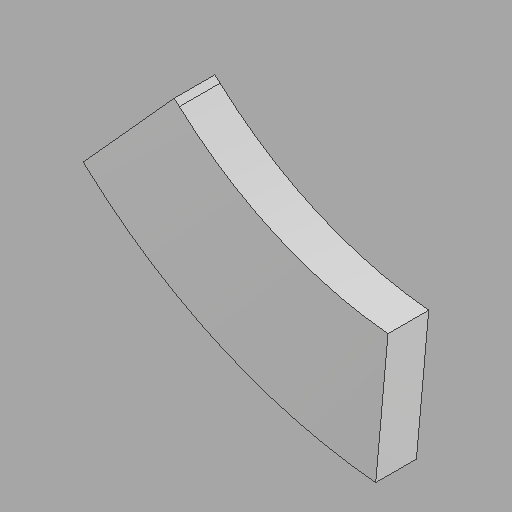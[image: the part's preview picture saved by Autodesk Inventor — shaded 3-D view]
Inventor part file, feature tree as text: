
AUTODESK INVENTOR PART (.ipt)
format: ipt  version: 2022.1 (Build 261234020, 234B)  size: 91,648 bytes
history: imported  units: in
note: dims shown in document units (in); Inventor stores cm internally (conversion verified against a paired STEP export)
features: imported_body x1
ambient origin geometry x8: Origin, YZ Plane, XZ Plane, XY Plane, X Axis, Y Axis, Z Axis, Center Point
bodies: Solid1 (imported_parasolid), Body1 (imported_parasolid)
feature tree (1):
  imported_body  NMx_Import_Brep_tag  [imported B-rep: ~8 faces, bbox_mm=[1140.794019, 868.777686, 152.4]]
